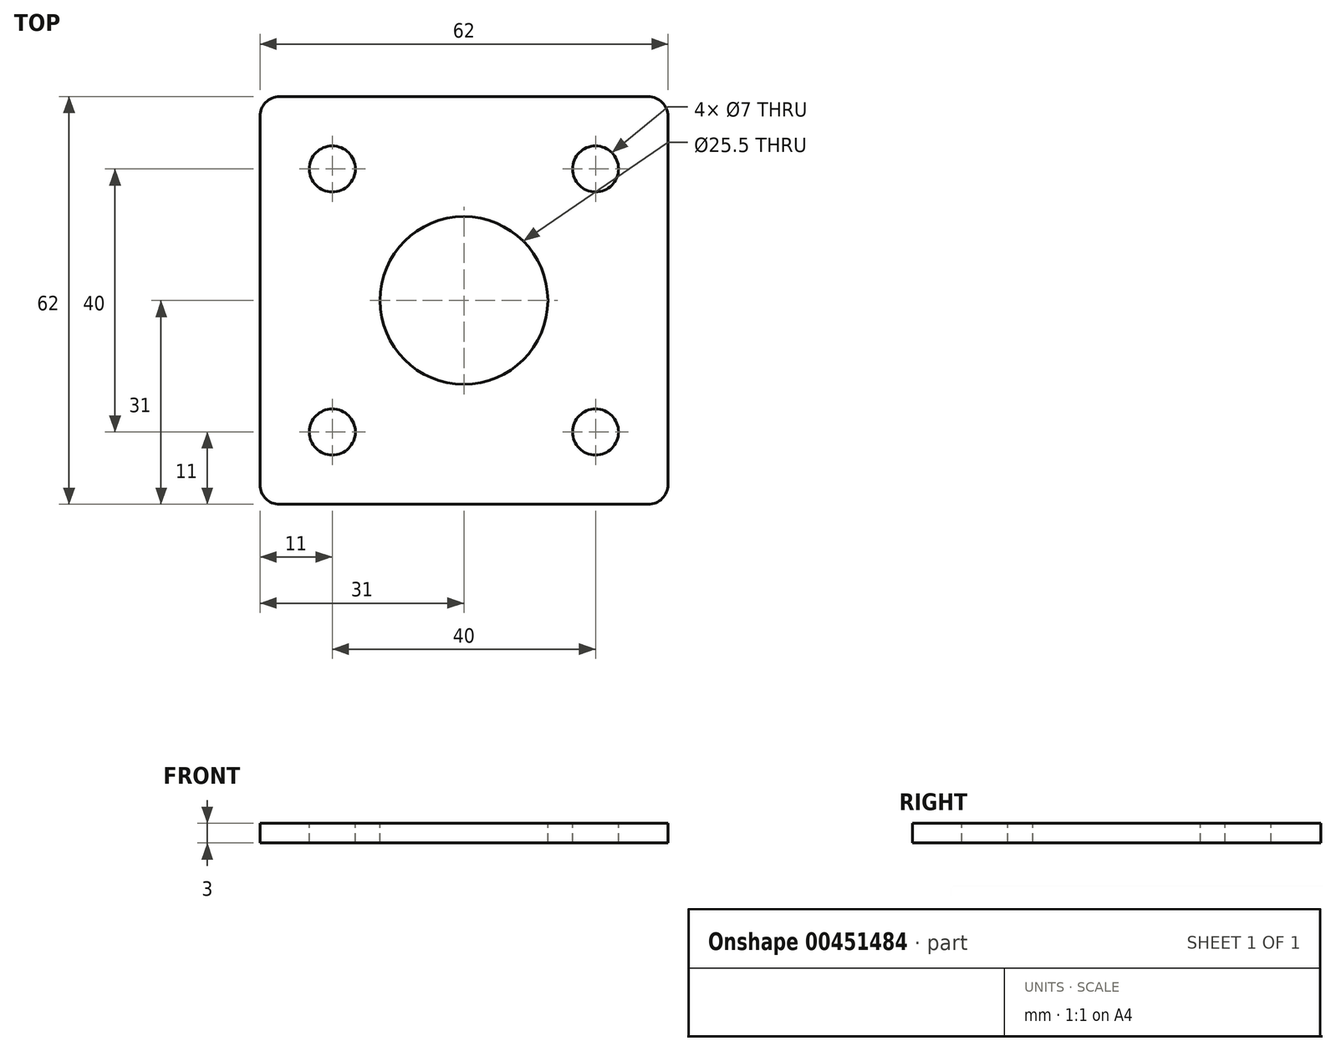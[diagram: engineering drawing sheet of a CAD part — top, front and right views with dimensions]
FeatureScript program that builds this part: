
annotation { "Feature Type Name" : "Feature", "Feature Type Description" : "" }
export const myFeature = defineFeature(function(context is Context, id is Id, definition is map)
    precondition{}
    {
        {
            var Q0;
            Q0=qCreatedBy(makeId("Top.planeOp"),FACE);
            var sketch = newSketch(context, id + "F0", { "sketchPlane" : qUnion([Q0])});
            skLineSegment(sketch, "E0.bottom", {"start": v(31, -31) * mm, "end": v(-31, -31) * mm});
            skLineSegment(sketch, "E0.top", {"start": v(31, 31) * mm, "end": v(-31, 31) * mm});
            skLineSegment(sketch, "E0.left", {"start": v(31, -31) * mm, "end": v(31, 31) * mm});
            skLineSegment(sketch, "E0.right", {"start": v(-31, -31) * mm, "end": v(-31, 31) * mm});
            skPoint(sketch, "E0.middle", {"position": v(0, 0) * mm});
            skSolve(sketch);
        }
        {
            var Q0;
            Q0=qSketchRegion(id+"F0",true);
            extrude(context, id + "F1", {"entities" : qUnion([Q0]), "depth" : 3 * mm});
        }
        {
            var Q0;
            Q0=makeQuery(id+"F1.opExtrude","CAP_FACE",FACE,{"disambiguationData":[OSD([sQuery(id+"F0.wireOp",EDGE,"E0.bottom"),sQuery(id+"F0.wireOp",EDGE,"E0.top"),sQuery(id+"F0.wireOp",EDGE,"E0.left"),sQuery(id+"F0.wireOp",EDGE,"E0.right")])],"isStart":false});
            var sketch = newSketch(context, id + "F2", { "sketchPlane" : qUnion([Q0])});
            skCircle(sketch, "E1", {"center": v(-20, 20) * mm, "radius": 3.5 * mm});
            skCircle(sketch, "E2.1.0", {"center": v(20, 20) * mm, "radius": 3.5 * mm});
            skCircle(sketch, "E2.2.0", {"center": v(20, -20) * mm, "radius": 3.5 * mm});
            skCircle(sketch, "E2.3.0", {"center": v(-20, -20) * mm, "radius": 3.5 * mm});
            skPoint(sketch, "E2.center", {"position": v(0, 0) * mm});
            skLineSegment(sketch, "E2.anchor1", {"start": v(0, 0) * mm, "end": v(-20, 20) * mm, "construction": true});
            skLineSegment(sketch, "E2.anchor2", {"start": v(0, 0) * mm, "end": v(-20, -20) * mm, "construction": true});
            skCircle(sketch, "E3", {"center": v(0, 0) * mm, "radius": 12.75 * mm});
            skSolve(sketch);
        }
        {
            var Q0;
            Q0=qSketchRegion(id+"F2",true);
            extrude(context, id + "F3", {"entities" : qUnion([Q0]), "operationType" : NewBodyOperationType.REMOVE, "oppositeDirection" : true, "depth" : 25 * mm});
        }
        {
            var Q0;
            Q0=makeQuery(id+"F1.opExtrude","SWEPT_EDGE",EDGE,{"disambiguationData":[OSD([sQuery(id+"F0.wireOp",EDGE,"E0.top"),sQuery(id+"F0.wireOp",EDGE,"E0.right")])]});
            var Q1;
            Q1=makeQuery(id+"F1.opExtrude","SWEPT_EDGE",EDGE,{"disambiguationData":[OSD([sQuery(id+"F0.wireOp",EDGE,"E0.top"),sQuery(id+"F0.wireOp",EDGE,"E0.left")])]});
            var Q2;
            Q2=makeQuery(id+"F1.opExtrude","SWEPT_EDGE",EDGE,{"disambiguationData":[OSD([sQuery(id+"F0.wireOp",EDGE,"E0.bottom"),sQuery(id+"F0.wireOp",EDGE,"E0.right")])]});
            var Q3;
            Q3=makeQuery(id+"F1.opExtrude","SWEPT_EDGE",EDGE,{"disambiguationData":[OSD([sQuery(id+"F0.wireOp",EDGE,"E0.bottom"),sQuery(id+"F0.wireOp",EDGE,"E0.left")])]});
            fillet(context, id + "F4", {"entities" : qUnion([Q0, Q1, Q2, Q3]), "radius" : 3 * mm, "tangentPropagation" : true, "allowEdgeOverflow" : false});
        }
    });
